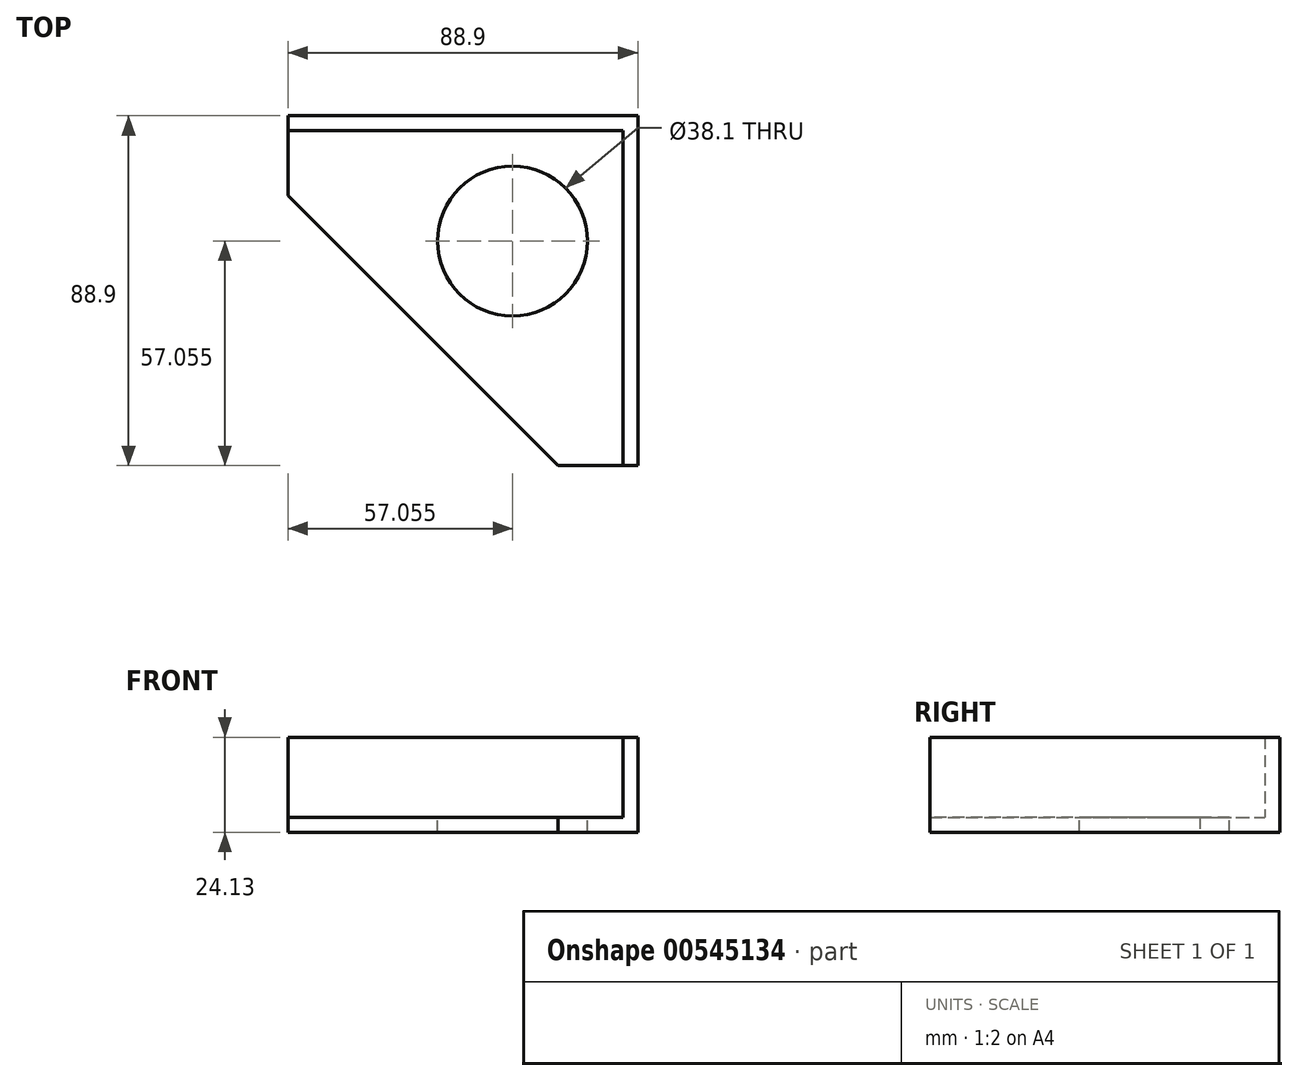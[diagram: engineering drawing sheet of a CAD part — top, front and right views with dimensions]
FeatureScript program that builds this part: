
annotation { "Feature Type Name" : "Feature", "Feature Type Description" : "" }
export const myFeature = defineFeature(function(context is Context, id is Id, definition is map)
    precondition{}
    {
        {
            var Q0;
            Q0=qCreatedBy(makeId("Top.planeOp"),FACE);
            var sketch = newSketch(context, id + "F0", { "sketchPlane" : qUnion([Q0])});
            skLineSegment(sketch, "E0.bottom", {"start": v(44.45, -44.45) * mm, "end": v(24.13, -44.45) * mm});
            skLineSegment(sketch, "E0.top", {"start": v(44.45, 44.45) * mm, "end": v(-44.45, 44.45) * mm});
            skLineSegment(sketch, "E0.left", {"start": v(44.45, -44.45) * mm, "end": v(44.45, 44.45) * mm});
            skLineSegment(sketch, "E0.right", {"start": v(-44.45, 24.13) * mm, "end": v(-44.45, 44.45) * mm});
            skPoint(sketch, "E0.middle", {"position": v(0, 0) * mm});
            skLineSegment(sketch, "E1", {"start": v(-44.45, 44.45) * mm, "end": v(-44.45, 24.13) * mm});
            skLineSegment(sketch, "E2", {"start": v(-44.45, 24.13) * mm, "end": v(24.13, -44.45) * mm});
            skPoint(sketch, "E3.orphan", {"position": v(-44.45, -44.45) * mm});
            skSolve(sketch);
        }
        {
            var Q0;
            Q0=makeQuery(id+"F0.imprint","IMPRINT",FACE,{"disambiguationData":[TD([[makeQuery(id+"F0.imprint","IMPRINT",EDGE,{"derivedFrom":sQuery(id+"F0.wireOp",EDGE,"E0.top")}),1.0]])]});
            extrude(context, id + "F1", {"entities" : qUnion([Q0]), "depth" : 3.8 * mm, "offsetDistance" : 25.4 * mm});
        }
        {
            var Q0;
            Q0=makeQuery(id+"F1.opExtrude","CAP_FACE",FACE,{"disambiguationData":[OSD([sQuery(id+"F0.wireOp",EDGE,"E0.top"),sQuery(id+"F0.wireOp",EDGE,"E0.left"),sQuery(id+"F0.wireOp",EDGE,"E1"),sQuery(id+"F0.wireOp",EDGE,"E0.bottom"),sQuery(id+"F0.wireOp",EDGE,"E2")])],"isStart":false});
            var sketch = newSketch(context, id + "F2", { "sketchPlane" : qUnion([Q0])});
            skLineSegment(sketch, "E4.bottom", {"start": v(-44.45, 44.45) * mm, "end": v(44.45, 44.45) * mm});
            skLineSegment(sketch, "E4.top", {"start": v(-44.45, 40.64) * mm, "end": v(40.64, 40.64) * mm});
            skLineSegment(sketch, "E4.left", {"start": v(-44.45, 44.45) * mm, "end": v(-44.45, 40.64) * mm});
            skLineSegment(sketch, "E4.right", {"start": v(44.45, 44.45) * mm, "end": v(44.45, 40.64) * mm});
            skLineSegment(sketch, "E5.bottom", {"start": v(44.45, -44.45) * mm, "end": v(40.64, -44.45) * mm});
            skLineSegment(sketch, "E5.top", {"start": v(44.45, 44.45) * mm, "end": v(40.64, 44.45) * mm});
            skLineSegment(sketch, "E5.left", {"start": v(44.45, -44.45) * mm, "end": v(44.45, 44.45) * mm});
            skLineSegment(sketch, "E5.right", {"start": v(40.64, -44.45) * mm, "end": v(40.64, 40.64) * mm});
            skSolve(sketch);
        }
        {
            var Q0;
            Q0=makeQuery(id+"F2.imprint","IMPRINT",FACE,{"disambiguationData":[TD([[makeQuery(id+"F2.imprint","IMPRINT",EDGE,{"derivedFrom":sQuery(id+"F2.wireOp",EDGE,"E4.bottom")}),1.0]])]});
            extrude(context, id + "F3", {"entities" : qUnion([Q0]), "operationType" : NewBodyOperationType.ADD, "depth" : 20.32 * mm, "offsetDistance" : 25.4 * mm});
        }
        {
            var Q0;
            Q0=makeQuery(id+"F1.opExtrude","CAP_FACE",FACE,{"disambiguationData":[OSD([sQuery(id+"F0.wireOp",EDGE,"E0.top"),sQuery(id+"F0.wireOp",EDGE,"E0.left"),sQuery(id+"F0.wireOp",EDGE,"E1"),sQuery(id+"F0.wireOp",EDGE,"E0.bottom"),sQuery(id+"F0.wireOp",EDGE,"E2")])],"isStart":false});
            var sketch = newSketch(context, id + "F4", { "sketchPlane" : qUnion([Q0])});
            skCircle(sketch, "E6", {"center": v(12.6, 12.6) * mm, "radius": 19.05 * mm});
            skSolve(sketch);
        }
        {
            var Q0;
            Q0=makeQuery(id+"F4.imprint","IMPRINT",FACE,{"disambiguationData":[TD([[makeQuery(id+"F4.imprint","IMPRINT",EDGE,{"derivedFrom":sQuery(id+"F4.wireOp",EDGE,"E6")}),1.0]])]});
            extrude(context, id + "F5", {"entities" : qUnion([Q0]), "operationType" : NewBodyOperationType.REMOVE, "oppositeDirection" : true, "depth" : 39.62 * mm, "offsetDistance" : 25.4 * mm});
        }
    });
